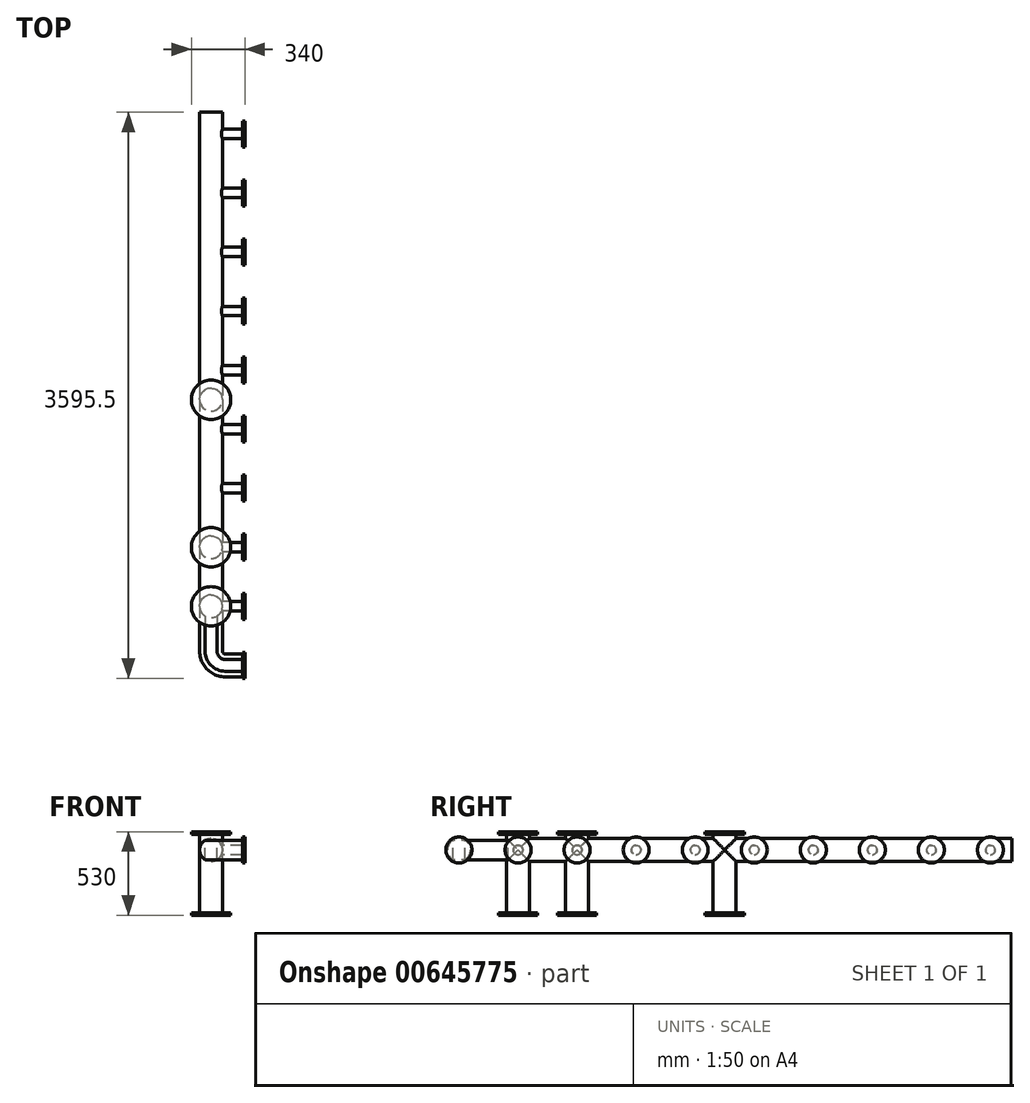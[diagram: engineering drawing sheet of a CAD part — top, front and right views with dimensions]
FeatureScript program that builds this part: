
annotation { "Feature Type Name" : "Feature", "Feature Type Description" : "" }
export const myFeature = defineFeature(function(context is Context, id is Id, definition is map)
    precondition{}
    {
        {
            var Q0;
            Q0=qCreatedBy(makeId("Front.planeOp"),FACE);
            var sketch = newSketch(context, id + "F0", { "sketchPlane" : qUnion([Q0])});
            skCircle(sketch, "E0", {"center": v(0, 0) * mm, "radius": 72.5 * mm});
            skSolve(sketch);
        }
        {
            var Q0;
            Q0=makeQuery(id+"F0.imprint","IMPRINT",FACE,{"disambiguationData":[TD([[makeQuery(id+"F0.imprint","IMPRINT",EDGE,{"derivedFrom":sQuery(id+"F0.wireOp",EDGE,"E0")}),1.0]])]});
            extrude(context, id + "F1", {"entities" : qUnion([Q0]), "oppositeDirection" : true, "depth" : 3200 * mm, "offsetDistance" : 25 * mm});
        }
        {
            var Q0;
            Q0=qCreatedBy(makeId("Right.planeOp"),FACE);
            var sketch = newSketch(context, id + "F2", { "sketchPlane" : qUnion([Q0])});
            skCircle(sketch, "E1", {"center": v(62.5, 0) * mm, "radius": 30 * mm});
            skCircle(sketch, "E2.1.0.0", {"center": v(437.5, 0) * mm, "radius": 30 * mm});
            skCircle(sketch, "E2.2.0.0", {"center": v(812.5, 0) * mm, "radius": 30 * mm});
            skCircle(sketch, "E2.3.0.0", {"center": v(1187.5, 0) * mm, "radius": 30 * mm});
            skCircle(sketch, "E2.4.0.0", {"center": v(1562.5, 0) * mm, "radius": 30 * mm});
            skCircle(sketch, "E2.5.0.0", {"center": v(1937.5, 0) * mm, "radius": 30 * mm});
            skCircle(sketch, "E2.6.0.0", {"center": v(2312.5, 0) * mm, "radius": 30 * mm});
            skCircle(sketch, "E2.7.0.0", {"center": v(2687.5, 0) * mm, "radius": 30 * mm});
            skCircle(sketch, "E2.8.0.0", {"center": v(3062.5, 0) * mm, "radius": 30 * mm});
            skLineSegment(sketch, "E2.direction1", {"start": v(62.5, 0) * mm, "end": v(437.5, 0) * mm, "construction": true});
            skSolve(sketch);
        }
        {
            var Q0;
            Q0=qSketchRegion(id+"F2",true);
            extrude(context, id + "F3", {"entities" : qUnion([Q0]), "operationType" : NewBodyOperationType.ADD, "depth" : 215 * mm, "offsetDistance" : 25 * mm});
        }
        {
            var Q0;
            Q0=makeQuery(id+"F3.opExtrude","CAP_FACE",FACE,{"disambiguationData":[OSD([sQuery(id+"F2.wireOp",EDGE,"E1")])],"isStart":false});
            var sketch = newSketch(context, id + "F4", { "sketchPlane" : qUnion([Q0])});
            skCircle(sketch, "E3", {"center": v(62.5, 0) * mm, "radius": 82.5 * mm});
            skCircle(sketch, "E4.1.0.0", {"center": v(437.5, 0) * mm, "radius": 82.5 * mm});
            skCircle(sketch, "E4.2.0.0", {"center": v(812.5, 0) * mm, "radius": 82.5 * mm});
            skCircle(sketch, "E4.3.0.0", {"center": v(1187.5, 0) * mm, "radius": 82.5 * mm});
            skCircle(sketch, "E4.4.0.0", {"center": v(1562.5, 0) * mm, "radius": 82.5 * mm});
            skCircle(sketch, "E4.5.0.0", {"center": v(1937.5, 0) * mm, "radius": 82.5 * mm});
            skCircle(sketch, "E4.6.0.0", {"center": v(2312.5, 0) * mm, "radius": 82.5 * mm});
            skCircle(sketch, "E4.7.0.0", {"center": v(2687.5, 0) * mm, "radius": 82.5 * mm});
            skCircle(sketch, "E4.8.0.0", {"center": v(3062.5, 0) * mm, "radius": 82.5 * mm});
            skLineSegment(sketch, "E4.direction1", {"start": v(62.5, 0) * mm, "end": v(437.5, 0) * mm, "construction": true});
            skSolve(sketch);
        }
        {
            var Q0;
            Q0=qSketchRegion(id+"F4",true);
            extrude(context, id + "F5", {"entities" : qUnion([Q0]), "operationType" : NewBodyOperationType.ADD, "oppositeDirection" : true, "depth" : 15 * mm, "offsetDistance" : 25 * mm});
        }
        {
            var Q0;
            Q0=qCreatedBy(makeId("Top.planeOp"),FACE);
            var sketch = newSketch(context, id + "F6", { "sketchPlane" : qUnion([Q0])});
            skCircle(sketch, "E5", {"center": v(0, 62) * mm, "radius": 72.5 * mm});
            skCircle(sketch, "E6.0.1.0", {"center": v(0, 437) * mm, "radius": 72.5 * mm});
            skLineSegment(sketch, "E6.direction1", {"start": v(0, 62) * mm, "end": v(25, 62) * mm, "construction": true});
            skLineSegment(sketch, "E6.direction2", {"start": v(0, 62) * mm, "end": v(0, 437) * mm, "construction": true});
            skSolve(sketch);
        }
        {
            var Q0;
            Q0=qSketchRegion(id+"F6",true);
            extrude(context, id + "F7", {"entities" : qUnion([Q0]), "operationType" : NewBodyOperationType.ADD, "oppositeDirection" : true, "depth" : 400 * mm, "offsetDistance" : 25 * mm});
        }
        {
            var Q0;
            Q0=makeQuery(id+"F7.opExtrude","CAP_FACE",FACE,{"disambiguationData":[OSD([sQuery(id+"F6.wireOp",EDGE,"E5")])],"isStart":false});
            var sketch = newSketch(context, id + "F8", { "sketchPlane" : qUnion([Q0])});
            skCircle(sketch, "E7", {"center": v(0, -62) * mm, "radius": 125 * mm});
            skCircle(sketch, "E8.0.1.0", {"center": v(0, -437) * mm, "radius": 125 * mm});
            skLineSegment(sketch, "E8.direction1", {"start": v(0, -62) * mm, "end": v(25, -62) * mm, "construction": true});
            skLineSegment(sketch, "E8.direction2", {"start": v(0, -62) * mm, "end": v(0, -437) * mm, "construction": true});
            skSolve(sketch);
        }
        {
            var Q0;
            Q0=qSketchRegion(id+"F8",true);
            extrude(context, id + "F9", {"entities" : qUnion([Q0]), "operationType" : NewBodyOperationType.ADD, "depth" : 15 * mm, "offsetDistance" : 25 * mm});
        }
        {
            var Q0;
            Q0=qCreatedBy(makeId("Top.planeOp"),FACE);
            var sketch = newSketch(context, id + "F10", { "sketchPlane" : qUnion([Q0])});
            skCircle(sketch, "E9", {"center": v(0, 1374.5) * mm, "radius": 72.5 * mm});
            skSolve(sketch);
        }
        {
            var Q0;
            Q0=qSketchRegion(id+"F10",true);
            extrude(context, id + "F11", {"entities" : qUnion([Q0]), "operationType" : NewBodyOperationType.ADD, "oppositeDirection" : true, "depth" : 400 * mm, "offsetDistance" : 25 * mm});
        }
        {
            var Q0;
            Q0=makeQuery(id+"F11.opExtrude","CAP_FACE",FACE,{"disambiguationData":[OSD([sQuery(id+"F10.wireOp",EDGE,"E9")])],"isStart":false});
            var sketch = newSketch(context, id + "F12", { "sketchPlane" : qUnion([Q0])});
            skCircle(sketch, "E10", {"center": v(0, -1374.5) * mm, "radius": 125 * mm});
            skSolve(sketch);
        }
        {
            var Q0;
            Q0=qSketchRegion(id+"F12",true);
            extrude(context, id + "F13", {"entities" : qUnion([Q0]), "operationType" : NewBodyOperationType.ADD, "depth" : 15 * mm, "offsetDistance" : 25 * mm});
        }
        {
            var Q0;
            Q0=qCreatedBy(makeId("Top.planeOp"),FACE);
            var sketch = newSketch(context, id + "F14", { "sketchPlane" : qUnion([Q0])});
            skCircle(sketch, "E11", {"center": v(0, 62) * mm, "radius": 72.5 * mm});
            skCircle(sketch, "E12.0.1.0", {"center": v(0, 437) * mm, "radius": 72.5 * mm});
            skLineSegment(sketch, "E12.direction1", {"start": v(0, 62) * mm, "end": v(25, 62) * mm, "construction": true});
            skLineSegment(sketch, "E12.direction2", {"start": v(0, 62) * mm, "end": v(0, 437) * mm, "construction": true});
            skCircle(sketch, "E13", {"center": v(0, 1374.5) * mm, "radius": 72.5 * mm});
            skSolve(sketch);
        }
        {
            var Q0;
            Q0=qSketchRegion(id+"F14",true);
            extrude(context, id + "F15", {"entities" : qUnion([Q0]), "operationType" : NewBodyOperationType.ADD, "depth" : 100 * mm, "offsetDistance" : 25 * mm});
        }
        {
            var Q0;
            Q0=makeQuery(id+"F15.opExtrude","CAP_FACE",FACE,{"disambiguationData":[OSD([sQuery(id+"F14.wireOp",EDGE,"E11")])],"isStart":false});
            var sketch = newSketch(context, id + "F16", { "sketchPlane" : qUnion([Q0])});
            skCircle(sketch, "E14", {"center": v(0, 62) * mm, "radius": 125 * mm});
            skCircle(sketch, "E15", {"center": v(0, 437) * mm, "radius": 125 * mm});
            skCircle(sketch, "E16", {"center": v(0, 1374) * mm, "radius": 125 * mm});
            skSolve(sketch);
        }
        {
            var Q0;
            Q0=qSketchRegion(id+"F16",true);
            extrude(context, id + "F17", {"entities" : qUnion([Q0]), "operationType" : NewBodyOperationType.ADD, "depth" : 15 * mm, "offsetDistance" : 25 * mm});
        }
        {
            var Q0;
            Q0=qCreatedBy(makeId("Top.planeOp"),FACE);
            var sketch = newSketch(context, id + "F18", { "sketchPlane" : qUnion([Q0])});
            skLineSegment(sketch, "E17", {"start": v(0, 0) * mm, "end": v(0, -223) * mm});
            skLineSegment(sketch, "E18", {"start": v(90, -313) * mm, "end": v(200, -313) * mm});
            skPoint(sketch, "E19.visualSharp", {"position": v(0, -313) * mm});
            skArc(sketch, "E19.filletArc", {"start": v(0, -223) * mm, "mid": v(26.36, -286.64) * mm, "end": v(90, -313) * mm});
            skSolve(sketch);
        }
        {
            var Q0;
            Q0=makeQuery(id+"F1.opExtrude","CAP_FACE",FACE,{"disambiguationData":[OSD([sQuery(id+"F0.wireOp",EDGE,"E0")])],"isStart":true});
            var Q1;
            Q1=sQuery(id+"F18.wireOp",EDGE,"E17");
            var Q2;
            Q2=sQuery(id+"F18.wireOp",EDGE,"E19.filletArc");
            var Q3;
            Q3=sQuery(id+"F18.wireOp",EDGE,"E18");
            sweep(context, id + "F19", {"operationType" : NewBodyOperationType.ADD, "profiles" : qUnion([Q0]), "path" : qUnion([Q1, Q2, Q3])});
        }
        {
            var Q0;
            Q0=makeQuery(id+"F19.opSweep","CAP_FACE",FACE,{"disambiguationData":[OSD([sQuery(id+"F0.wireOp",EDGE,"E0"),sQuery(id+"F18.wireOp",VERTEX,"E18.end")])],"isStart":false});
            var sketch = newSketch(context, id + "F20", { "sketchPlane" : qUnion([Q0])});
            skCircle(sketch, "E20", {"center": v(-313, 0) * mm, "radius": 82.5 * mm});
            skSolve(sketch);
        }
        {
            var Q0;
            Q0=qSketchRegion(id+"F20",true);
            extrude(context, id + "F21", {"entities" : qUnion([Q0]), "operationType" : NewBodyOperationType.ADD, "depth" : 15 * mm, "offsetDistance" : 25 * mm});
        }
    });
